# Revit family: ПКНВ-50А
name_source: partatom
category: Арматура трубопроводов
units: mm (PartAtom-declared; Revit-internal decimal feet)

## family parameters
Всегда вертикально = Да
На основе рабочей плоскости = Нет
Общий = Нет
При загрузке вырезать с полостями = Нет
Размер круглого соединителя = Использовать диаметр
Тип детали = Клапан - Вставляется

## types (2) — shared parameters
ADSK_Диапазон контролируемого давления, МПа = 0,0016-0,6
ADSK_Единица измерения = шт.
ADSK_Завод-изготовитель = РУП "БЕЛГАЗТЕХНИКА"
ADSK_Количество = 1
ADSK_Максимальное входное давление, МПа = 1,2
ADSK_Марка = ПКНВ-50А
ADSK_Масса_Текст = 25,2 кг
ADSK_Тип соединения = фланцевое
ADSK_Тип управляющего сигнала = электрический
zero-valued in all types: Отметка по умолчанию

## per-type parameters (varying)
| type | ADSK_Наименование | исполнение 06 | исполнение 07 |
| исполнение 06 | Клапан ПКНВ-50А-06  ТУ РБ 00555028-012-94 | Да | Нет |
| исполнение 07 | Клапан ПКНВ-50А-07  ТУ РБ 00555028-012-94 | Нет | Да |
